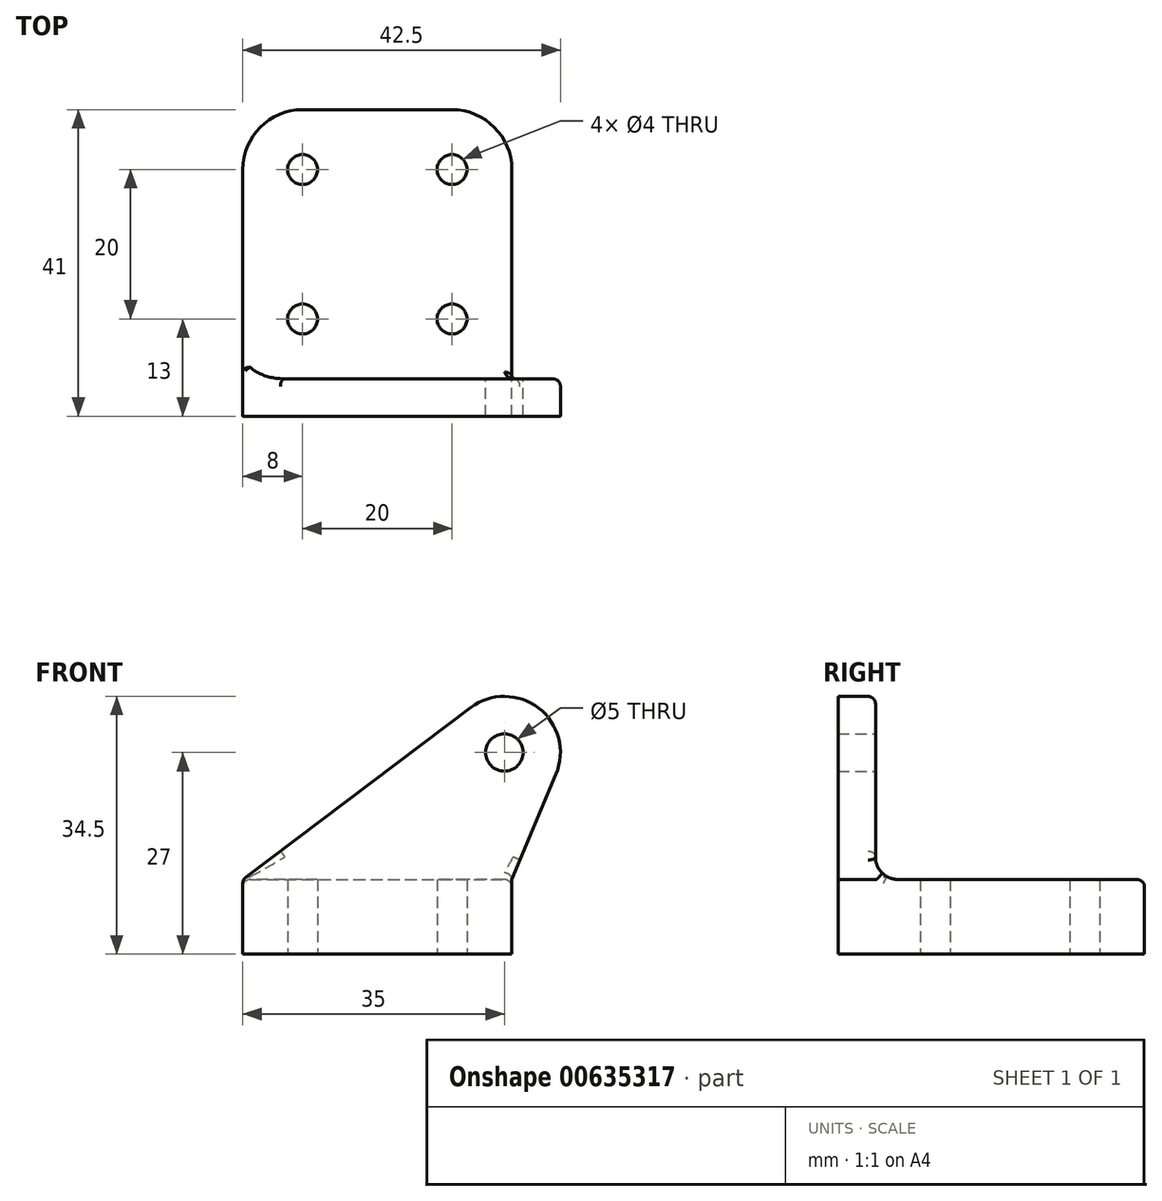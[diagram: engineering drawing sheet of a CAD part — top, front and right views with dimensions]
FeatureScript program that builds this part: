
annotation { "Feature Type Name" : "Feature", "Feature Type Description" : "" }
export const myFeature = defineFeature(function(context is Context, id is Id, definition is map)
    precondition{}
    {
        {
            var Q0;
            Q0=qCreatedBy(makeId("Top.planeOp"),FACE);
            var sketch = newSketch(context, id + "F0", { "sketchPlane" : qUnion([Q0])});
            skLineSegment(sketch, "E0.bottom", {"start": v(-20, 8) * mm, "end": v(0, 8) * mm, "construction": true});
            skLineSegment(sketch, "E0.top", {"start": v(-20, 28) * mm, "end": v(0, 28) * mm, "construction": true});
            skLineSegment(sketch, "E0.left", {"start": v(-20, 8) * mm, "end": v(-20, 28) * mm, "construction": true});
            skLineSegment(sketch, "E0.right", {"start": v(0, 8) * mm, "end": v(0, 28) * mm, "construction": true});
            skCircle(sketch, "E1", {"center": v(-20, 8) * mm, "radius": 2 * mm});
            skCircle(sketch, "E2", {"center": v(-20, 28) * mm, "radius": 2 * mm});
            skCircle(sketch, "E3", {"center": v(0, 8) * mm, "radius": 2 * mm});
            skCircle(sketch, "E4", {"center": v(0, 28) * mm, "radius": 2 * mm});
            skLineSegment(sketch, "E5.bottom", {"start": v(-28, 0) * mm, "end": v(8, 0) * mm});
            skLineSegment(sketch, "E5.top", {"start": v(-20, 36) * mm, "end": v(0, 36) * mm});
            skLineSegment(sketch, "E5.left", {"start": v(-28, 0) * mm, "end": v(-28, 28) * mm});
            skLineSegment(sketch, "E5.right", {"start": v(8, 0) * mm, "end": v(8, 28) * mm});
            skArc(sketch, "E6.filletArc", {"start": v(-20, 36) * mm, "mid": v(-25.66, 33.66) * mm, "end": v(-28, 28) * mm});
            skArc(sketch, "E7.filletArc", {"start": v(8, 28) * mm, "mid": v(5.66, 33.66) * mm, "end": v(0, 36) * mm});
            skSolve(sketch);
        }
        {
            var Q0;
            Q0=makeQuery(id+"F0.imprint","IMPRINT",FACE,{"disambiguationData":[TD([[makeQuery(id+"F0.imprint","IMPRINT",EDGE,{"derivedFrom":sQuery(id+"F0.wireOp",EDGE,"E1")}),-1.0]])]});
            extrude(context, id + "F1", {"entities" : qUnion([Q0]), "depth" : 10 * mm, "offsetDistance" : 25 * mm});
        }
        {
            var Q0;
            Q0=qCreatedBy(makeId("Front.planeOp"),FACE);
            var sketch = newSketch(context, id + "F2", { "sketchPlane" : qUnion([Q0])});
            skArc(sketch, "E8", {"start": v(13.92, 24.1) * mm, "mid": v(11.6, 32.92) * mm, "end": v(2.48, 32.99) * mm});
            skCircle(sketch, "E9", {"center": v(7, 27) * mm, "radius": 2.5 * mm});
            skLineSegment(sketch, "E10", {"start": v(2.48, 32.99) * mm, "end": v(-28, 10) * mm});
            skLineSegment(sketch, "E11", {"start": v(-28, 10) * mm, "end": v(8, 10) * mm});
            skLineSegment(sketch, "E12", {"start": v(8, 10) * mm, "end": v(13.92, 24.1) * mm});
            skSolve(sketch);
        }
        {
            var Q0;
            Q0=makeQuery(id+"F2.imprint","IMPRINT",FACE,{"disambiguationData":[TD([[makeQuery(id+"F2.imprint","IMPRINT",EDGE,{"derivedFrom":sQuery(id+"F2.wireOp",EDGE,"E8")}),1.0]])]});
            extrude(context, id + "F3", {"entities" : qUnion([Q0]), "depth" : 5 * mm, "offsetDistance" : 25 * mm});
        }
        {
            var Q0;
            Q0=makeQuery(id+"F3.opExtrude","SWEPT_FACE",FACE,{"disambiguationData":[OSD([sQuery(id+"F2.wireOp",EDGE,"E11")])]});
            extrude(context, id + "F4", {"entities" : qUnion([Q0]), "depth" : 10 * mm, "offsetDistance" : 25 * mm});
        }
        {
            var Q0;
            Q0=makeQuery(id+"F3.opExtrude","SWEPT_BODY",BODY,{"disambiguationData":[OSD([sQuery(id+"F2.wireOp",EDGE,"E8"),sQuery(id+"F2.wireOp",EDGE,"E9"),sQuery(id+"F2.wireOp",EDGE,"E10"),sQuery(id+"F2.wireOp",EDGE,"E11"),sQuery(id+"F2.wireOp",EDGE,"E12")])]});
            var Q1;
            Q1=makeQuery(id+"F4.opExtrude","SWEPT_BODY",BODY,{"disambiguationData":[OSD([sQuery(id+"F2.wireOp",EDGE,"E11")])]});
            var Q2;
            Q2=makeQuery(id+"F1.opExtrude","SWEPT_BODY",BODY,{"disambiguationData":[OSD([sQuery(id+"F0.wireOp",EDGE,"E1"),sQuery(id+"F0.wireOp",EDGE,"E2"),sQuery(id+"F0.wireOp",EDGE,"E3"),sQuery(id+"F0.wireOp",EDGE,"E4"),sQuery(id+"F0.wireOp",EDGE,"E5.bottom"),sQuery(id+"F0.wireOp",EDGE,"E5.top"),sQuery(id+"F0.wireOp",EDGE,"E5.left"),sQuery(id+"F0.wireOp",EDGE,"E5.right"),sQuery(id+"F0.wireOp",EDGE,"E6.filletArc"),sQuery(id+"F0.wireOp",EDGE,"E7.filletArc")])]});
            booleanBodies(context, id + "F5", {"operationType" : BooleanOperationType.UNION, "tools" : qUnion([Q0, Q1, Q2])});
        }
        {
            var Q0;
            Q0=makeQuery(id+"F3.opExtrude","CAP_EDGE",EDGE,{"disambiguationData":[OSD([sQuery(id+"F2.wireOp",EDGE,"E11")])],"isStart":true});
            fillet(context, id + "F6", {"entities" : qUnion([Q0]), "radius" : 3 * mm, "tangentPropagation" : true, "allowEdgeOverflow" : false});
        }
        {
            var Q0;
            Q0=makeQuery(id+"F5.opBoolean","MERGE",EDGE,{"derivedFrom":[makeQuery(id+"F1.opExtrude","CAP_EDGE",EDGE,{"disambiguationData":[OSD([sQuery(id+"F0.wireOp",EDGE,"E5.right")])],"isStart":false}),makeQuery(id+"F4.opExtrude","CAP_EDGE",EDGE,{"disambiguationData":[OSD([sQuery(id+"F2.wireOp",EDGE,"E11"),sQuery(id+"F2.wireOp",EDGE,"E12")])],"isStart":true})]});
            var Q1;
            Q1=makeQuery(id+"F3.opExtrude","CAP_EDGE",EDGE,{"disambiguationData":[OSD([sQuery(id+"F2.wireOp",EDGE,"E12")])],"isStart":true});
            fillet(context, id + "F7", {"entities" : qUnion([Q0, Q1]), "radius" : 1 * mm, "tangentPropagation" : true, "allowEdgeOverflow" : false});
        }
        {
            var Q0;
            {var subQ0=sQuery(id+"F2.wireOp",EDGE,"E11");var subQ1=sQuery(id+"F2.wireOp",EDGE,"E10");Q0=makeQuery(id+"F5.opBoolean","MERGE",EDGE,{"derivedFrom":[makeQuery(id+"F1.opExtrude","CAP_EDGE",EDGE,{"disambiguationData":[OSD([sQuery(id+"F0.wireOp",EDGE,"E5.left")])],"isStart":false}),makeQuery(id+"F3.opExtrude","SWEPT_EDGE",EDGE,{"disambiguationData":[OSD([subQ1,subQ0])]}),makeQuery(id+"F4.opExtrude","CAP_EDGE",EDGE,{"disambiguationData":[OSD([subQ1,subQ0])],"isStart":true})]});}
            var Q1;
            {var subQ0=sQuery(id+"F2.wireOp",EDGE,"E10");Q1=makeQuery(id+"F7.opFillet","BLEND_EDGE",EDGE,{"blendedFrom":[makeQuery(id+"F5.opBoolean","MERGE",EDGE,{"derivedFrom":[makeQuery(id+"F1.opExtrude","CAP_EDGE",EDGE,{"disambiguationData":[OSD([sQuery(id+"F0.wireOp",EDGE,"E5.left")])],"isStart":false}),makeQuery(id+"F4.opExtrude","CAP_EDGE",EDGE,{"disambiguationData":[OSD([subQ0,sQuery(id+"F2.wireOp",EDGE,"E11")])],"isStart":true})]}),makeQuery(id+"F3.opExtrude","SWEPT_FACE",FACE,{"disambiguationData":[OSD([subQ0])]})],"blendedInto":[makeQuery(id+"F3.opExtrude","SWEPT_FACE",FACE,{"disambiguationData":[OSD([subQ0])]})]});}
            fillet(context, id + "F8", {"entities" : qUnion([Q0, Q1]), "radius" : 1 * mm, "tangentPropagation" : true, "allowEdgeOverflow" : false});
        }
    });
